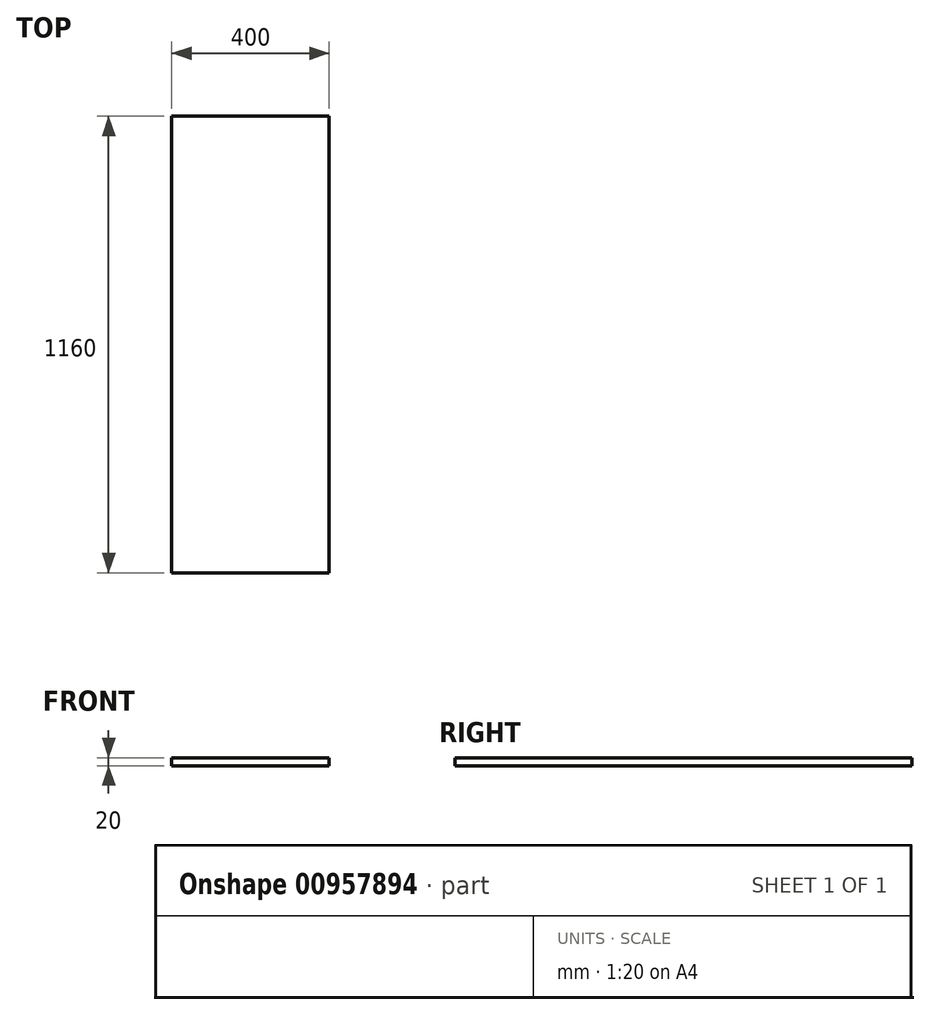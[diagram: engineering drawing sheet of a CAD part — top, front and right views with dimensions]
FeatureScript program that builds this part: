
annotation { "Feature Type Name" : "Feature", "Feature Type Description" : "" }
export const myFeature = defineFeature(function(context is Context, id is Id, definition is map)
    precondition{}
    {
        {
            var Q0;
            Q0=qCreatedBy(makeId("Top.planeOp"),FACE);
            var sketch = newSketch(context, id + "F0", { "sketchPlane" : qUnion([Q0])});
            skLineSegment(sketch, "E0.bottom", {"start": v(200, -580) * mm, "end": v(-200, -580) * mm});
            skLineSegment(sketch, "E0.top", {"start": v(200, 580) * mm, "end": v(-200, 580) * mm});
            skLineSegment(sketch, "E0.left", {"start": v(200, -580) * mm, "end": v(200, 580) * mm});
            skLineSegment(sketch, "E0.right", {"start": v(-200, -580) * mm, "end": v(-200, 580) * mm});
            skPoint(sketch, "E0.middle", {"position": v(0, 0) * mm});
            skSolve(sketch);
        }
        {
            var Q0;
            Q0=makeQuery(id+"F0.imprint","IMPRINT",FACE,{"disambiguationData":[TD([[makeQuery(id+"F0.imprint","IMPRINT",EDGE,{"derivedFrom":sQuery(id+"F0.wireOp",EDGE,"E0.bottom")}),-1.0]])]});
            extrude(context, id + "F1", {"entities" : qUnion([Q0]), "depth" : 20 * mm, "offsetDistance" : 25.4 * mm});
        }
    });
